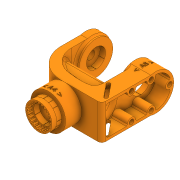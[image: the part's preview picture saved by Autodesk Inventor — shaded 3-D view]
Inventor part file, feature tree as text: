
AUTODESK INVENTOR PART (.ipt)
format: ipt  version: 2020 (Build 240168000, 168)  size: 2,148,352 bytes
history: native  units: in
note: dims shown in document units (in); Inventor stores cm internally (conversion verified against a paired STEP export)
features: sketch x41, extrude x37, projected_geometry x29, chamfer x8, fillet x8, plane x6, emboss x3
ambient origin geometry x8: Origin, YZ Plane, XZ Plane, XY Plane, X Axis, Y Axis, Z Axis, Center Point
bodies: Solid1 (feature_tree)
feature tree (132):
  extrude  "Extrusion1"  Depth=2.0472in
  extrude  "Extrusion2"  Depth=1.1063in
  chamfer  "Chamfer2"  Distance=0.2756in
  extrude  "Extrusion4"  Depth=0.0157in
  extrude  "Extrusion7"  Depth=0.2756in TaperAngle=0.0deg
  chamfer  "Chamfer4"  Distance=0.0394in
  extrude  "Extrusion8"  Depth=0.0157in
  sketch  "Sketch12"  dims[d39=1.4567in d57=0.0394in d58=0.0in]
  plane  "Work Plane1"
  sketch  "Sketch13"  dims[d59=0.315in d60=0.125in d61=0.0137in d67=0.0157in]
  extrude  "Extrusion10"  Depth=0.0394in TaperAngle=0.0deg
  extrude  "Extrusion11"  Depth=0.0866in
  chamfer  "Chamfer5"  Distance=9.4488in Angle=360.0deg
  extrude  "Extrusion12"  Depth=0.2756in TaperAngle=0.0deg
  plane  "Work Plane2"
  extrude  "Extrusion13"  Depth=0.315in
  plane  "Work Plane3"
  extrude  "Extrusion14"  Depth=1.0236in
  extrude  "Extrusion15"  Depth=0.8858in
  extrude  "Extrusion16"  Depth=0.3937in
  extrude  "Extrusion17"  Depth=1.378in
  sketch  "Sketch21"  dims[d107=0.315in d108=0.0in d109=0.315in d110=0.125in d111=0.0137in]
  extrude  "Extrusion19"  Depth=0.5906in
  sketch  "Sketch23"  dims[d112=1.0in d113=0.0in d114=1.0236in]
  extrude  "Extrusion20"  Depth=0.1575in TaperAngle=0.0deg
  extrude  "Extrusion21"  Depth=0.1575in TaperAngle=0.0deg
  extrude  "Extrusion22"  Depth=4.2323in
  extrude  "Extrusion23"  Depth=0.1575in
  extrude  "Extrusion24"  Depth=1.1024in
  extrude  "Extrusion25"  Depth=0.4921in
  extrude  "Extrusion26"  Depth=0.75in
  extrude  "Extrusion27"  Depth=0.2165in TaperAngle=0.0deg
  extrude  "Extrusion28"  Depth=0.1575in
  extrude  "Extrusion29"  Depth=1.1811in
  plane  "Work Plane4"
  extrude  "Extrusion30"  Depth=0.3937in TaperAngle=0.0deg
  fillet  "Fillet1"  Radius=0.3937in
  fillet  "Fillet2"  Radius=0.315in
  extrude  "Extrusion31"  Depth=0.315in TaperAngle=0.0deg
  extrude  "Extrusion32"  Depth=0.315in TaperAngle=0.0deg
  extrude  "Extrusion33"  Depth=0.3937in TaperAngle=0.0deg
  fillet  "Fillet3"  Radius=0.2165in
  extrude  "Extrusion34"  Depth=0.4724in
  chamfer  "Chamfer6"  Distance=0.2756in
  chamfer  "Chamfer7"  Distance=0.0394in
  extrude  "Extrusion35"  Depth=0.001in
  extrude  "Extrusion36"  Depth=1.0in TaperAngle=0.0deg
  fillet  "Fillet5"  Radius=0.1575in
  extrude  "Extrusion38"  Depth=0.315in
  extrude  "Extrusion39"  Depth=0.1969in
  extrude  "Extrusion40"  Depth=0.1969in TaperAngle=360.0deg
  fillet  "Fillet7"  Radius=1.0in
  extrude  "Extrusion41"  Depth=0.1969in TaperAngle=0.0deg
  chamfer  "Chamfer8"  Distance=0.1969in
  extrude  "Extrusion42"  Depth=0.3937in TaperAngle=0.0deg
  plane  "Work Plane6"
  emboss  "Emboss1"
  emboss  "Emboss2"
  plane  "Work Plane7"
  emboss  "Emboss3"
  extrude  "Extrusion43"  Depth=0.1969in
  fillet  "Fillet9"  Radius=0.0787in
  fillet  "Fillet10"  Radius=0.1969in
  chamfer  "Chamfer9"  Distance=0.1181in
  fillet  "Fillet11"  Radius=1.0039in
  chamfer  "Chamfer10"  Distance=0.4134in
  sketch  "Sketch1"  dims[d0=0.6299in d1=2.0472in]
  sketch  "Sketch2"  dims[d2=0.9449in d3=0.0in d4=1.1063in]
  sketch  "Sketch4"  dims[d5=1.5748in d6=0.2756in d7=0.0in]
  sketch  "Sketch8"  dims[d11=0.2756in d12=0.125in d13=0.0137in d25=0.0157in]
  projected_geometry  "Projected Loop2"
  sketch  "Sketch10"  dims[d26=6.2992in d28=360.0deg d30=0.2756in d31=0.0in]
  sketch  "Sketch14"  dims[d68=4.7244in d70=360.0deg d72=0.0394in d73=0.0in]
  sketch  "Sketch15"  dims[d83=0.0591in d84=0.0866in]
  projected_geometry  "Projected Loop4"
  sketch  "Sketch16"  dims[d85=0.0827in]
  sketch  "Sketch17"  dims[d86=0.0827in]
  projected_geometry  "Projected Loop5"
  sketch  "Sketch18"  dims[d87=0.0827in d88=9.4488in d90=360.0deg]
  projected_geometry  "Projected Loop6"
  projected_geometry  "Projected Loop7"
  sketch  "Sketch19"  dims[d92=0.2756in]
  projected_geometry  "Projected Loop8"
  projected_geometry  "Projected Loop9"
  sketch  "Sketch20"  dims[d94=9.4488in d95=0.0827in d96=0.0827in d97=0.0827in d98=360.0deg d105=0.2756in d106=0.0in]
  projected_geometry  "Projected Loop10"
  projected_geometry  "Projected Loop11"
  projected_geometry  "Projected Loop12"
  projected_geometry  "Projected Loop13"
  sketch  "Sketch25"  dims[d115=0.7874in d117=0.8858in]
  sketch  "Sketch26"  dims[d118=2.7559in d119=0.3937in]
  projected_geometry  "Projected Loop16"
  projected_geometry  "Projected Loop17"
  sketch  "Sketch27"  dims[d120=0.5906in d121=1.378in]
  projected_geometry  "Projected Loop18"
  projected_geometry  "Projected Loop19"
  sketch  "Sketch28"  dims[d123=3.4941in d124=0.5906in]
  projected_geometry  "Projected Loop20"
  projected_geometry  "Projected Loop21"
  sketch  "Sketch29"  dims[d126=1.9685in d129=0.1575in d130=0.0in]
  projected_geometry  "Projected Loop22"
  projected_geometry  "Projected Loop23"
  sketch  "Sketch30"  dims[d131=-2.0472in d132=0.1575in d133=0.0in]
  projected_geometry  "Projected Loop24"
  sketch  "Sketch31"  dims[d134=2.126in d136=4.2323in]
  sketch  "Sketch32"  dims[d137=0.1575in d138=0.1575in]
  sketch  "Sketch34"  dims[d139=0.4921in d140=0.0in d141=1.1024in]
  projected_geometry  "Projected Loop25"
  sketch  "Sketch35"  dims[d142=1.1614in d143=0.4921in]
  sketch  "Sketch36"  dims[d144=0.3445in d145=0.75in]
  projected_geometry  "Projected Loop26"
  sketch  "Sketch37"  dims[d146=0.1575in d147=0.0in d148=0.2165in d149=0.0in]
  projected_geometry  "Projected Loop27"
  sketch  "Sketch38"  dims[d152=1.0039in d153=0.0in d154=0.1575in]
  projected_geometry  "Projected Loop28"
  sketch  "Sketch39"  dims[d155=0.1575in d160=1.1811in]
  projected_geometry  "Projected Loop29"
  sketch  "Sketch40"  dims[d161=0.1969in d162=0.0in d163=0.315in d164=0.0in d165=0.3937in d166=0.0in d167=0.315in d168=0.0in]
  sketch  "Sketch41"  dims[d169=0.315in d170=0.0in d171=0.315in d172=0.0in]
  projected_geometry  "Projected Loop30"
  sketch  "Sketch43"  dims[d173=0.315in d174=0.0in d175=0.315in d176=0.0in]
  projected_geometry  "Projected Loop31"
  sketch  "Sketch44"  dims[d177=1.1024in d178=0.3937in d179=0.0in d180=0.2165in d181=0.0in]
  sketch  "Sketch45"  dims[d183=-0.0197in d184=0.4724in d185=0.2756in d186=0.0in]
  sketch  "Sketch46"  dims[d187=0.5512in]
  projected_geometry  "Projected Loop32"
  sketch  "Sketch47"  dims[d188=0.2165in d189=0.0394in d190=0.0in]
  projected_geometry  "Projected Loop33"
  sketch  "Sketch48"  dims[d191=0.0394in d192=0.0in d193=0.001in]
  sketch  "Sketch49"  dims[d194=0.001in d195=1.0in d196=0.0in d197=0.1575in]
  sketch  "Sketch50"  dims[d198=1.0in d199=0.0in d200=0.315in d201=0.125in d202=0.0137in]
  sketch  "Sketch52"  dims[d203=0.315in d204=0.125in d205=0.0137in d206=0.0157in d207=2.3622in d209=360.0deg d211=1.0in d212=0.0in d213=1.0in d214=0.0in d221=0.1969in d222=0.3937in d223=0.0in d224=0.1575in d225=0.0787in d226=0.1969in d227=0.0in d229=0.1181in d230=1.0039in d231=0.4134in d232=0.5118in d233=0.0984in d235=0.0197in d236=0.1181in d237=0.1181in d238=0.2047in d239=0.2047in d240=0.0in d241=0.0in d242=0.2362in d243=0.0787in d244=0.0787in d251=0.0787in d252=0.0787in d253=0.2756in d254=0.4724in d255=0.2756in d256=0.4724in d257=0.2756in d258=0.4724in d259=0.2756in d260=0.4724in d261=0.1575in d262=0.0in d263=0.0787in d264=0.125in d265=45.0deg d266=1.0in d267=0.0in d269=0.0394in d270=0.0in d271=0.0394in d272=0.0in d273=0.0394in d274=0.0in d275=0.0039in d276=0.0787in d277=1.0in d278=0.0in d279=0.122in d280=0.2361in d282=0.1378in d283=0.2047in d284=0.1575in d285=0.125in d286=45.0deg d287=0.1575in d288=0.0394in d289=0.125in d290=45.0deg]
